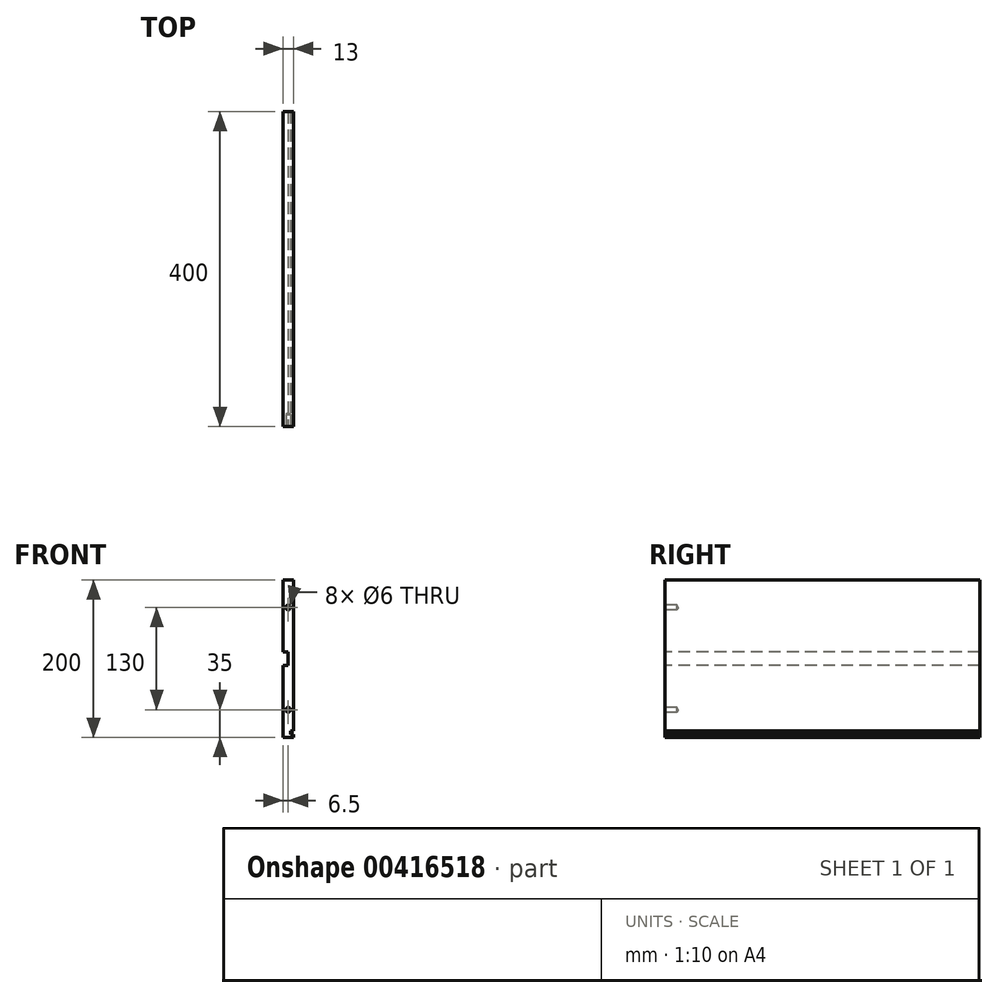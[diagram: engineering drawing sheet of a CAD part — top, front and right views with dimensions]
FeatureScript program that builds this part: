
annotation { "Feature Type Name" : "Feature", "Feature Type Description" : "" }
export const myFeature = defineFeature(function(context is Context, id is Id, definition is map)
    precondition{}
    {
        {
            var Q0;
            Q0=qCreatedBy(makeId("Front.planeOp"),FACE);
            var sketch = newSketch(context, id + "F0", { "sketchPlane" : qUnion([Q0])});
            skLineSegment(sketch, "E0.bottom", {"start": v(-6.5, 100) * mm, "end": v(6.5, 100) * mm});
            skLineSegment(sketch, "E0.top", {"start": v(-6.5, -100) * mm, "end": v(6.5, -100) * mm});
            skLineSegment(sketch, "E0.left", {"start": v(-6.5, 100) * mm, "end": v(-6.5, 8.5) * mm});
            skLineSegment(sketch, "E0.right", {"start": v(6.5, 100) * mm, "end": v(6.5, -92) * mm});
            skPoint(sketch, "E0.middle", {"position": v(0, 0) * mm});
            skLineSegment(sketch, "E1", {"start": v(-6.5, -8.5) * mm, "end": v(-6.5, -100) * mm});
            skLineSegment(sketch, "E2", {"start": v(-6.5, 8.5) * mm, "end": v(-0.5, 8.5) * mm});
            skLineSegment(sketch, "E3", {"start": v(-0.5, 8.5) * mm, "end": v(-0.5, -8.5) * mm});
            skLineSegment(sketch, "E4", {"start": v(-0.5, -8.5) * mm, "end": v(-6.5, -8.5) * mm});
            skLineSegment(sketch, "E5", {"start": v(6.5, -96) * mm, "end": v(2.88, -96) * mm});
            skLineSegment(sketch, "E6", {"start": v(2.88, -96) * mm, "end": v(2.88, -92) * mm});
            skLineSegment(sketch, "E7", {"start": v(2.88, -92) * mm, "end": v(6.5, -92) * mm});
            skLineSegment(sketch, "E8", {"start": v(6.5, -96) * mm, "end": v(6.5, -100) * mm});
            skSolve(sketch);
        }
        {
            var Q0;
            Q0 = qSketchRegion(id + "F0", true);
            extrude(context, id + "F1", {"entities" : qUnion([Q0]), "endBound" : BoundingType.SYMMETRIC, "oppositeDirection" : true, "depth" : 400 * mm});
        }
        {
            var Q0;
            Q0=makeQuery(id+"F1.opExtrude","CAP_FACE",FACE,{"disambiguationData":[OSD([sQuery(id+"F0.wireOp",EDGE,"E0.bottom"),sQuery(id+"F0.wireOp",EDGE,"E0.top"),sQuery(id+"F0.wireOp",EDGE,"E0.left"),sQuery(id+"F0.wireOp",EDGE,"E0.right"),sQuery(id+"F0.wireOp",EDGE,"E1"),sQuery(id+"F0.wireOp",EDGE,"E2"),sQuery(id+"F0.wireOp",EDGE,"E3"),sQuery(id+"F0.wireOp",EDGE,"E4"),sQuery(id+"F0.wireOp",EDGE,"E5"),sQuery(id+"F0.wireOp",EDGE,"E6"),sQuery(id+"F0.wireOp",EDGE,"E7"),sQuery(id+"F0.wireOp",EDGE,"E8")])],"isStart":true});
            var sketch = newSketch(context, id + "F2", { "sketchPlane" : qUnion([Q0])});
            skPoint(sketch, "E9", {"position": v(0, 65) * mm});
            skPoint(sketch, "E10", {"position": v(0, -65) * mm});
            skSolve(sketch);
        }
        {
            var Q0;
            Q0=sQuery(id+"F2.wireOp",VERTEX,"E9");
            var Q1;
            Q1=sQuery(id+"F2.wireOp",VERTEX,"E10");
            var Q2;
            Q2=makeQuery(id+"F1.opExtrude","SWEPT_BODY",BODY,{"disambiguationData":[OSD([sQuery(id+"F0.wireOp",EDGE,"E0.bottom"),sQuery(id+"F0.wireOp",EDGE,"E0.top"),sQuery(id+"F0.wireOp",EDGE,"E0.left"),sQuery(id+"F0.wireOp",EDGE,"E0.right"),sQuery(id+"F0.wireOp",EDGE,"E1"),sQuery(id+"F0.wireOp",EDGE,"E2"),sQuery(id+"F0.wireOp",EDGE,"E3"),sQuery(id+"F0.wireOp",EDGE,"E4"),sQuery(id+"F0.wireOp",EDGE,"E5"),sQuery(id+"F0.wireOp",EDGE,"E6"),sQuery(id+"F0.wireOp",EDGE,"E7"),sQuery(id+"F0.wireOp",EDGE,"E8")])]});
            hole(context, id + "F3", {"style" : HoleStyle.SIMPLE, "endStyle" : HoleEndStyle.BLIND, "holeDiameter" : 6 * mm, "holeDepth" : 15 * mm, "isTappedThrough" : true, "tappedDepth" : 12 * mm, "tapClearance" : 3, "startFromSketch" : true, "locations" : qUnion([Q0, Q1]), "scope" : qUnion([Q2])});
        }
    });
